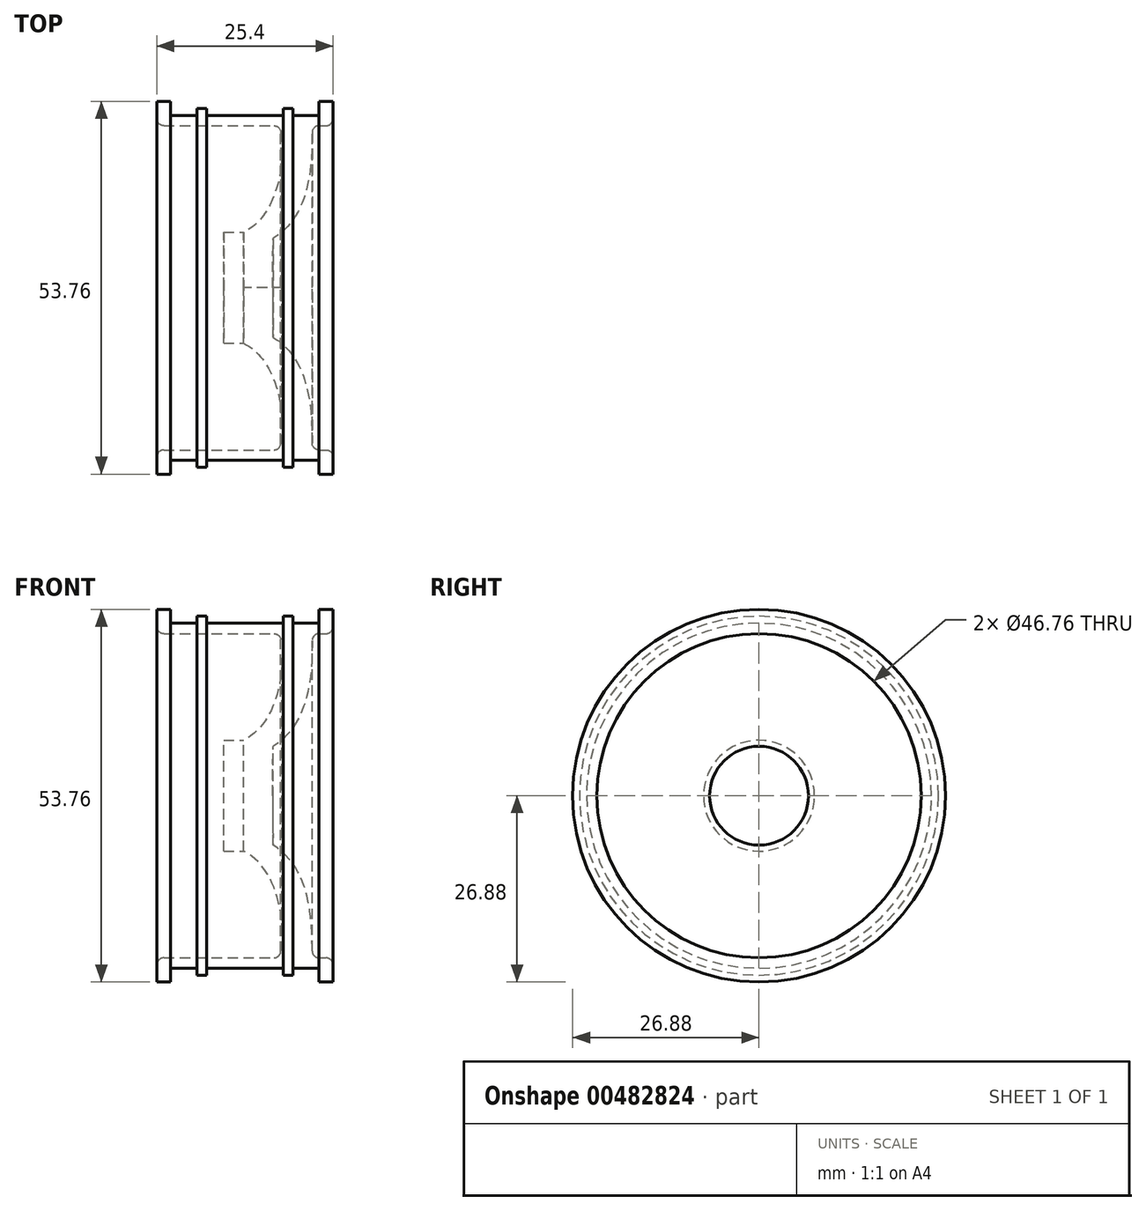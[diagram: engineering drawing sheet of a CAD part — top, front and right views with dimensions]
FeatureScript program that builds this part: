
annotation { "Feature Type Name" : "Feature", "Feature Type Description" : "" }
export const myFeature = defineFeature(function(context is Context, id is Id, definition is map)
    precondition{}
    {
        {
            var Q0;
            Q0=qCreatedBy(makeId("Front.planeOp"),FACE);
            var sketch = newSketch(context, id + "F0", { "sketchPlane" : qUnion([Q0])});
            skLineSegment(sketch, "E0", {"start": v(0, 0) * mm, "end": v(0, 8) * mm});
            skLineSegment(sketch, "E1", {"start": v(0, 8) * mm, "end": v(2.87, 8) * mm});
            skLineSegment(sketch, "E2", {"start": v(7.24, 23.38) * mm, "end": v(-8.65, 23.38) * mm});
            skLineSegment(sketch, "E3", {"start": v(-9.65, 24.38) * mm, "end": v(-9.65, 26.88) * mm});
            skLineSegment(sketch, "E4", {"start": v(-9.65, 26.88) * mm, "end": v(-7.65, 26.88) * mm});
            skLineSegment(sketch, "E5", {"start": v(-7.65, 26.88) * mm, "end": v(-7.65, 24.88) * mm});
            skLineSegment(sketch, "E6", {"start": v(-7.65, 24.88) * mm, "end": v(-3.85, 24.88) * mm});
            skLineSegment(sketch, "E7", {"start": v(-3.85, 24.88) * mm, "end": v(-3.85, 25.88) * mm});
            skLineSegment(sketch, "E8", {"start": v(-3.85, 25.88) * mm, "end": v(-2.45, 25.88) * mm});
            skLineSegment(sketch, "E9", {"start": v(-2.45, 25.88) * mm, "end": v(-2.45, 24.88) * mm});
            skLineSegment(sketch, "E10", {"start": v(-2.45, 24.88) * mm, "end": v(8.55, 24.88) * mm});
            skLineSegment(sketch, "E11", {"start": v(8.55, 24.88) * mm, "end": v(8.55, 25.88) * mm});
            skLineSegment(sketch, "E12", {"start": v(8.55, 25.88) * mm, "end": v(9.95, 25.88) * mm});
            skLineSegment(sketch, "E13", {"start": v(9.95, 25.88) * mm, "end": v(9.95, 24.88) * mm});
            skLineSegment(sketch, "E14", {"start": v(9.95, 24.88) * mm, "end": v(13.75, 24.88) * mm});
            skLineSegment(sketch, "E15", {"start": v(13.75, 24.88) * mm, "end": v(13.75, 26.88) * mm});
            skLineSegment(sketch, "E16", {"start": v(13.75, 26.88) * mm, "end": v(15.75, 26.88) * mm});
            skLineSegment(sketch, "E17", {"start": v(15.75, 26.88) * mm, "end": v(15.75, 24.38) * mm});
            skLineSegment(sketch, "E18", {"start": v(14.75, 23.38) * mm, "end": v(13.75, 23.38) * mm});
            skLineSegment(sketch, "E19", {"start": v(7.05, 0) * mm, "end": v(0, 0) * mm});
            skFitSpline(sketch, "E20", {"points": [v(8.08, 23.38) * mm, v(2.87, 8) * mm], "startDerivative": vector(3.08, -15.04) * mm, "endDerivative": vector(-14.93, -7.5) * mm});
            skFitSpline(sketch, "E21", {"points": [v(12.75, 23.38) * mm, v(7.05, 7.1) * mm], "startDerivative": vector(0, -15.04) * mm, "endDerivative": vector(-17.1, -10.22) * mm});
            skLineSegment(sketch, "E22", {"start": v(7.1, 7.12) * mm, "end": v(7.05, 0) * mm});
            skArc(sketch, "E23.filletArc", {"start": v(13.75, 23.38) * mm, "mid": v(13.05, 23.1) * mm, "end": v(12.75, 22.39) * mm});
            skArc(sketch, "E24.filletArc", {"start": v(8.23, 22.53) * mm, "mid": v(7.89, 23.14) * mm, "end": v(7.24, 23.38) * mm});
            skPoint(sketch, "E25.visualSharp", {"position": v(-9.65, 23.38) * mm});
            skArc(sketch, "E25.filletArc", {"start": v(-9.65, 24.38) * mm, "mid": v(-9.35, 23.67) * mm, "end": v(-8.65, 23.38) * mm});
            skPoint(sketch, "E26.visualSharp", {"position": v(15.75, 23.38) * mm});
            skArc(sketch, "E26.filletArc", {"start": v(14.75, 23.38) * mm, "mid": v(15.46, 23.67) * mm, "end": v(15.75, 24.38) * mm});
            skSolve(sketch);
        }
        {
            var Q0;
            Q0=makeQuery(id+"F0.imprint","IMPRINT",FACE,{"disambiguationData":[TD([[makeQuery(id+"F0.imprint","IMPRINT",EDGE,{"derivedFrom":sQuery(id+"F0.wireOp",EDGE,"E0")}),-1.0]])]});
            var Q1;
            Q1=sQuery(id+"F0.wireOp",EDGE,"E19");
            revolve(context, id + "F1", {"entities" : qUnion([Q0]), "axis" : qUnion([Q1]), "revolveType" : RevolveType.FULL});
        }
    });
